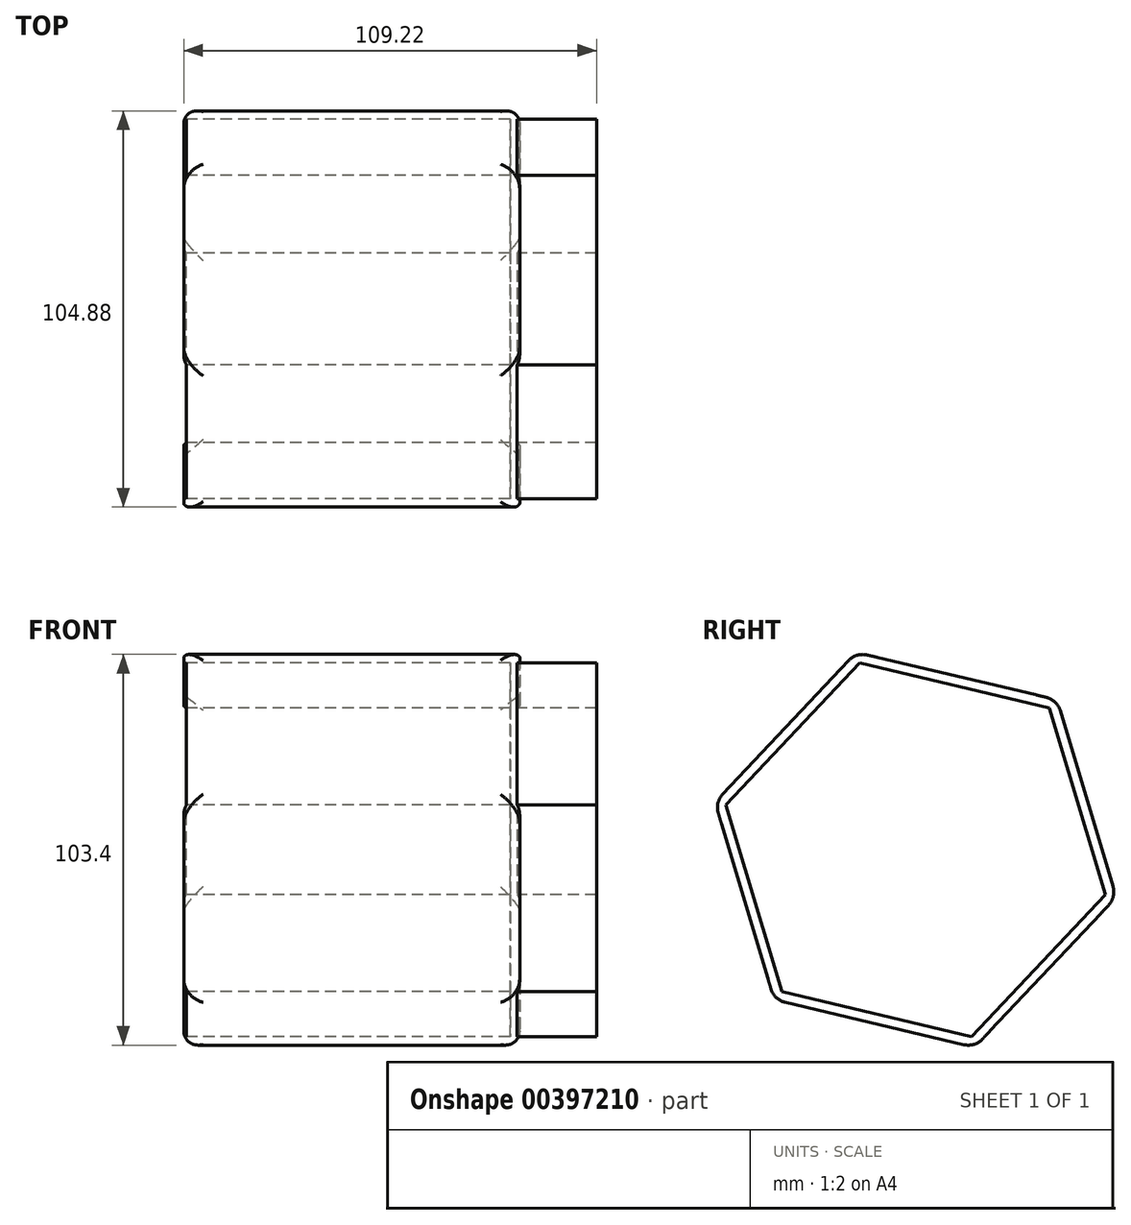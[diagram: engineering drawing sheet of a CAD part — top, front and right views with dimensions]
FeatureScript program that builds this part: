
annotation { "Feature Type Name" : "Feature", "Feature Type Description" : "" }
export const myFeature = defineFeature(function(context is Context, id is Id, definition is map)
    precondition{}
    {
        {
            var Q0;
            Q0=qCreatedBy(makeId("Right.planeOp"),FACE);
            var sketch = newSketch(context, id + "F0", { "sketchPlane" : qUnion([Q0])});
            skCircle(sketch, "E0.cCircle", {"center": v(0, 0) * mm, "radius": 47.23 * mm, "construction": true});
            skLineSegment(sketch, "E0.0", {"start": v(-53.07, 12.56) * mm, "end": v(-15.66, 52.24) * mm});
            skLineSegment(sketch, "E0.1", {"start": v(-15.66, 52.24) * mm, "end": v(37.4, 39.68) * mm});
            skLineSegment(sketch, "E0.2", {"start": v(37.4, 39.68) * mm, "end": v(53.07, -12.56) * mm});
            skLineSegment(sketch, "E0.3", {"start": v(53.07, -12.56) * mm, "end": v(15.66, -52.24) * mm});
            skLineSegment(sketch, "E0.4", {"start": v(15.66, -52.24) * mm, "end": v(-37.4, -39.68) * mm});
            skLineSegment(sketch, "E0.5", {"start": v(-37.4, -39.68) * mm, "end": v(-53.07, 12.56) * mm});
            skPoint(sketch, "E0.0.midPoint", {"position": v(-34.36, 32.4) * mm});
            skSolve(sketch);
        }
        {
            var Q0;
            Q0=makeQuery(id+"F0.imprint","IMPRINT",FACE,{"disambiguationData":[TD([[makeQuery(id+"F0.imprint","IMPRINT",EDGE,{"derivedFrom":sQuery(id+"F0.wireOp",EDGE,"E0.0")}),-1.0]])]});
            extrude(context, id + "F1", {"entities" : qUnion([Q0]), "depth" : 88.9 * mm});
        }
        {
            var Q0;
            Q0=makeQuery(id+"F1.opExtrude","CAP_FACE",FACE,{"disambiguationData":[OSD([sQuery(id+"F0.wireOp",EDGE,"E0.0"),sQuery(id+"F0.wireOp",EDGE,"E0.1"),sQuery(id+"F0.wireOp",EDGE,"E0.2"),sQuery(id+"F0.wireOp",EDGE,"E0.3"),sQuery(id+"F0.wireOp",EDGE,"E0.4"),sQuery(id+"F0.wireOp",EDGE,"E0.5")])],"isStart":true});
            shell(context, id + "F2", {"entities" : qUnion([Q0]), "thickness" : 2.54 * mm});
        }
        {
            var Q0;
            Q0=makeQuery(id+"F1.opExtrude","SWEPT_FACE",FACE,{"disambiguationData":[OSD([sQuery(id+"F0.wireOp",EDGE,"E0.0")])]});
            fillet(context, id + "F3", {"entities" : qUnion([Q0]), "radius" : 5.08 * mm, "tangentPropagation" : true, "allowEdgeOverflow" : false});
        }
        {
            var Q0;
            Q0=makeQuery(id+"F1.opExtrude","SWEPT_FACE",FACE,{"disambiguationData":[OSD([sQuery(id+"F0.wireOp",EDGE,"E0.2")])]});
            fillet(context, id + "F4", {"entities" : qUnion([Q0]), "radius" : 5.08 * mm, "tangentPropagation" : true, "allowEdgeOverflow" : false});
        }
        {
            var Q0;
            Q0=makeQuery(id+"F1.opExtrude","SWEPT_FACE",FACE,{"disambiguationData":[OSD([sQuery(id+"F0.wireOp",EDGE,"E0.4")])]});
            fillet(context, id + "F5", {"entities" : qUnion([Q0]), "radius" : 5.08 * mm, "tangentPropagation" : true, "allowEdgeOverflow" : false});
        }
        {
            var Q0;
            Q0=makeQuery(id+"F2.opShell","OFFSET_FACE",FACE,{"disambiguationData":[OSD([sQuery(id+"F0.wireOp",EDGE,"E0.0"),sQuery(id+"F0.wireOp",EDGE,"E0.1"),sQuery(id+"F0.wireOp",EDGE,"E0.2"),sQuery(id+"F0.wireOp",EDGE,"E0.3"),sQuery(id+"F0.wireOp",EDGE,"E0.4"),sQuery(id+"F0.wireOp",EDGE,"E0.5")])]});
            extrude(context, id + "F6", {"entities" : qUnion([Q0]), "operationType" : NewBodyOperationType.ADD, "oppositeDirection" : true, "depth" : 22.86 * mm});
        }
    });
